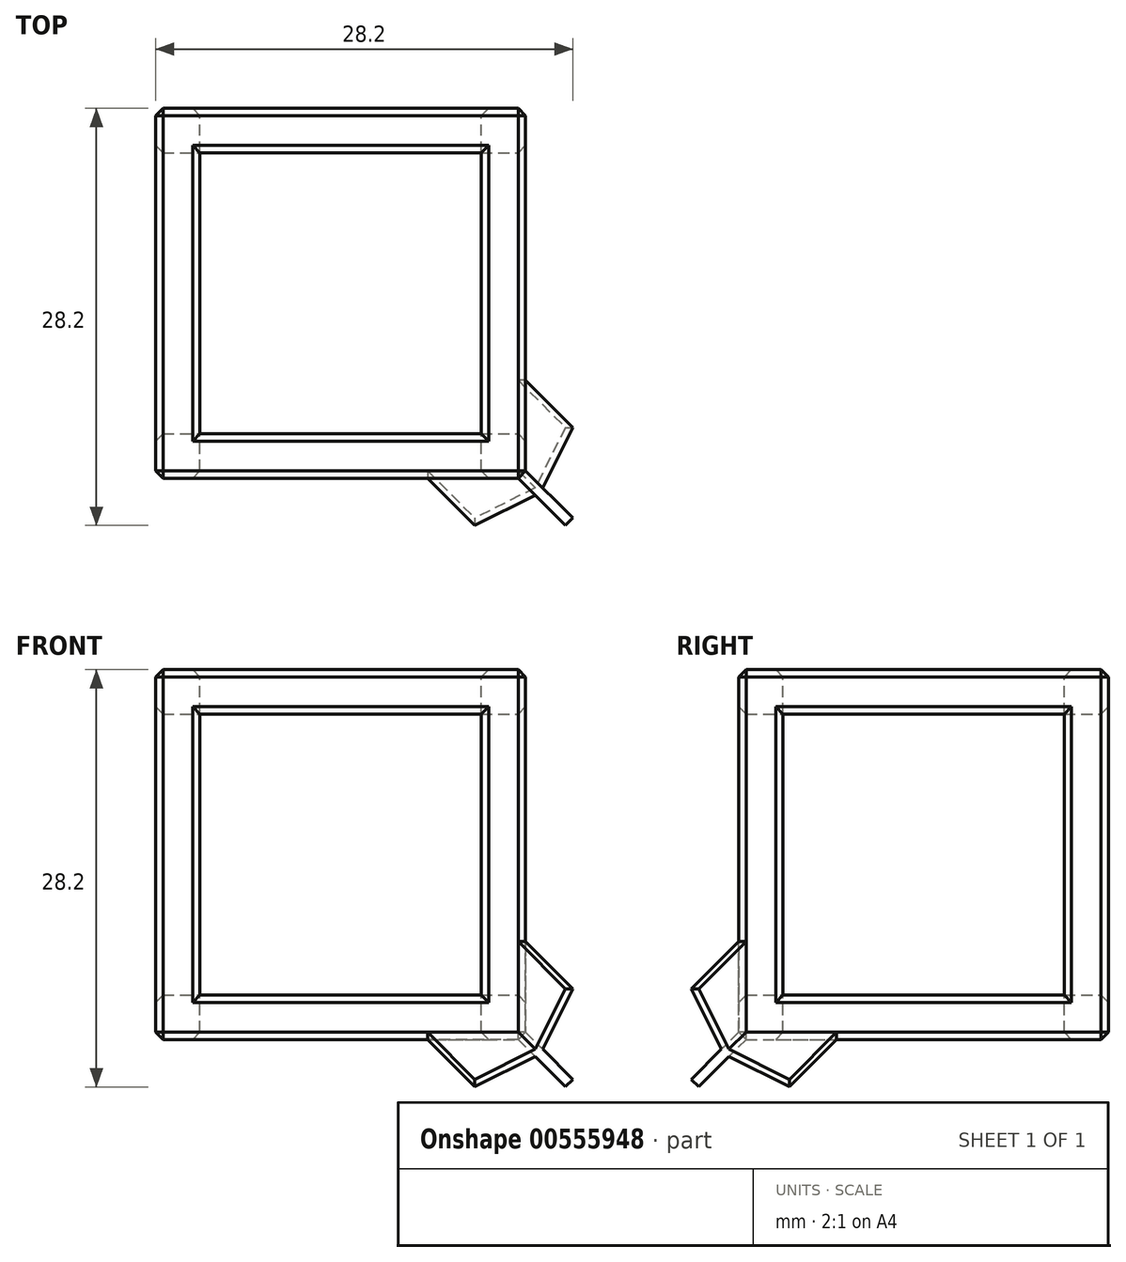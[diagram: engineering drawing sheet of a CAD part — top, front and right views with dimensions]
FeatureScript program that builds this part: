
annotation { "Feature Type Name" : "Feature", "Feature Type Description" : "" }
export const myFeature = defineFeature(function(context is Context, id is Id, definition is map)
    precondition{}
    {
        {
            var Q0;
            Q0=qCreatedBy(makeId("Front.planeOp"),FACE);
            var sketch = newSketch(context, id + "F0", { "sketchPlane" : qUnion([Q0])});
            skLineSegment(sketch, "E0.bottom", {"start": v(12.5, -12.5) * mm, "end": v(-12.5, -12.5) * mm});
            skLineSegment(sketch, "E0.top", {"start": v(12.5, 12.5) * mm, "end": v(-12.5, 12.5) * mm});
            skLineSegment(sketch, "E0.left", {"start": v(12.5, -12.5) * mm, "end": v(12.5, 12.5) * mm});
            skLineSegment(sketch, "E0.right", {"start": v(-12.5, -12.5) * mm, "end": v(-12.5, 12.5) * mm});
            skPoint(sketch, "E0.middle", {"position": v(0, 0) * mm});
            skLineSegment(sketch, "E1.0", {"start": v(9.5, -9.5) * mm, "end": v(-9.5, -9.5) * mm});
            skLineSegment(sketch, "E1.1", {"start": v(9.5, -9.5) * mm, "end": v(9.5, 9.5) * mm});
            skLineSegment(sketch, "E1.2", {"start": v(9.5, 9.5) * mm, "end": v(-9.5, 9.5) * mm});
            skLineSegment(sketch, "E1.3", {"start": v(-9.5, -9.5) * mm, "end": v(-9.5, 9.5) * mm});
            skSolve(sketch);
        }
        {
            var Q0;
            Q0=makeQuery(id+"F0.imprint","IMPRINT",FACE,{"disambiguationData":[TD([[makeQuery(id+"F0.imprint","IMPRINT",EDGE,{"derivedFrom":sQuery(id+"F0.wireOp",EDGE,"E0.bottom")}),-1.0]])]});
            extrude(context, id + "F1", {"entities" : qUnion([Q0]), "depth" : 12.5 * mm, "offsetDistance" : 25 * mm, "hasSecondDirection" : true, "secondDirectionOppositeDirection" : true, "secondDirectionDepth" : 12.5 * mm});
        }
        {
            var Q0;
            Q0=qCreatedBy(makeId("Right.planeOp"),FACE);
            var sketch = newSketch(context, id + "F2", { "sketchPlane" : qUnion([Q0])});
            skLineSegment(sketch, "E2.0", {"start": v(9.5, -9.5) * mm, "end": v(9.5, 9.5) * mm});
            skLineSegment(sketch, "E2.1", {"start": v(-9.5, -9.5) * mm, "end": v(9.5, -9.5) * mm});
            skLineSegment(sketch, "E2.2", {"start": v(-9.5, 9.5) * mm, "end": v(-9.5, -9.5) * mm});
            skLineSegment(sketch, "E2.3", {"start": v(9.5, 9.5) * mm, "end": v(-9.5, 9.5) * mm});
            skSolve(sketch);
        }
        {
            var Q0;
            Q0=makeQuery(id+"F2.imprint","IMPRINT",FACE,{"disambiguationData":[TD([[makeQuery(id+"F2.imprint","IMPRINT",EDGE,{"derivedFrom":sQuery(id+"F2.wireOp",EDGE,"E2.0")}),1.0]])]});
            extrude(context, id + "F3", {"entities" : qUnion([Q0]), "operationType" : NewBodyOperationType.REMOVE, "oppositeDirection" : true, "depth" : 25 * mm, "offsetDistance" : 25 * mm, "hasSecondDirection" : true, "secondDirectionOppositeDirection" : false, "secondDirectionDepth" : 25 * mm});
        }
        {
            var Q0;
            Q0=qCreatedBy(makeId("Top.planeOp"),FACE);
            var sketch = newSketch(context, id + "F4", { "sketchPlane" : qUnion([Q0])});
            skLineSegment(sketch, "E3.0", {"start": v(9.5, 9.5) * mm, "end": v(-9.5, 9.5) * mm});
            skLineSegment(sketch, "E3.1", {"start": v(9.5, -9.5) * mm, "end": v(9.5, 9.5) * mm});
            skLineSegment(sketch, "E3.2", {"start": v(-9.5, -9.5) * mm, "end": v(9.5, -9.5) * mm});
            skLineSegment(sketch, "E3.3", {"start": v(-9.5, 9.5) * mm, "end": v(-9.5, -9.5) * mm});
            skSolve(sketch);
        }
        {
            var Q0;
            Q0=makeQuery(id+"F4.imprint","IMPRINT",FACE,{"disambiguationData":[TD([[makeQuery(id+"F4.imprint","IMPRINT",EDGE,{"derivedFrom":sQuery(id+"F4.wireOp",EDGE,"E3.0")}),1.0]])]});
            extrude(context, id + "F5", {"entities" : qUnion([Q0]), "operationType" : NewBodyOperationType.REMOVE, "oppositeDirection" : true, "depth" : 25 * mm, "offsetDistance" : 25 * mm, "hasSecondDirection" : true, "secondDirectionOppositeDirection" : false, "secondDirectionDepth" : 25 * mm});
        }
        {
            var Q0;
            Q0=makeQuery(id+"F1.opExtrude","SWEPT_FACE",FACE,{"disambiguationData":[OSD([sQuery(id+"F0.wireOp",EDGE,"E0.left")])]});
            var Q1;
            Q1=makeQuery(id+"F1.opExtrude","SWEPT_FACE",FACE,{"disambiguationData":[OSD([sQuery(id+"F0.wireOp",EDGE,"E0.top")])]});
            var Q2;
            Q2=makeQuery(id+"F1.opExtrude","CAP_FACE",FACE,{"disambiguationData":[OSD([sQuery(id+"F0.wireOp",EDGE,"E0.bottom"),sQuery(id+"F0.wireOp",EDGE,"E0.top"),sQuery(id+"F0.wireOp",EDGE,"E0.left"),sQuery(id+"F0.wireOp",EDGE,"E0.right"),sQuery(id+"F0.wireOp",EDGE,"E1.0"),sQuery(id+"F0.wireOp",EDGE,"E1.1"),sQuery(id+"F0.wireOp",EDGE,"E1.2"),sQuery(id+"F0.wireOp",EDGE,"E1.3")])],"isStart":false});
            var Q3;
            Q3=makeQuery(id+"F1.opExtrude","CAP_FACE",FACE,{"disambiguationData":[OSD([sQuery(id+"F0.wireOp",EDGE,"E0.bottom"),sQuery(id+"F0.wireOp",EDGE,"E0.top"),sQuery(id+"F0.wireOp",EDGE,"E0.left"),sQuery(id+"F0.wireOp",EDGE,"E0.right"),sQuery(id+"F0.wireOp",EDGE,"E1.0"),sQuery(id+"F0.wireOp",EDGE,"E1.1"),sQuery(id+"F0.wireOp",EDGE,"E1.2"),sQuery(id+"F0.wireOp",EDGE,"E1.3")])],"isStart":true});
            var Q4;
            Q4=makeQuery(id+"F1.opExtrude","SWEPT_FACE",FACE,{"disambiguationData":[OSD([sQuery(id+"F0.wireOp",EDGE,"E0.right")])]});
            var Q5;
            Q5=makeQuery(id+"F1.opExtrude","SWEPT_FACE",FACE,{"disambiguationData":[OSD([sQuery(id+"F0.wireOp",EDGE,"E0.bottom")])]});
            chamfer(context, id + "F6", {"entities" : qUnion([Q0, Q1, Q2, Q3, Q4, Q5]), "width" : .5 * mm, "tangentPropagation" : true});
        }
        {
            var Q0;
            {var subQ0=sQuery(id+"F0.wireOp",EDGE,"E0.left");var subQ1=sQuery(id+"F0.wireOp",EDGE,"E0.bottom");Q0=makeQuery(id+"F6.opChamfer","BLEND_FACE",FACE,{"disambiguationData":[OSD([subQ1,subQ0]),TDD([makeQuery(id+"F1.opExtrude","CAP_VERTEX",VERTEX,{"disambiguationData":[OSD([subQ1,subQ0])],"isStart":false})])]});}
            cPlane(context, id + "F7", {"entities" : qUnion([Q0]), "cplaneType" : CPlaneType.OFFSET, "offset" : 2 * mm, "width" : 150 * mm, "height" : 150 * mm});
        }
        {
            var Q0;
            Q0=qCreatedBy(id+"F7.planeOp",FACE);
            var sketch = newSketch(context, id + "F8", { "sketchPlane" : qUnion([Q0])});
            skLineSegment(sketch, "E4.0", {"start": v(0.4, 0) * mm, "end": v(10.2, -16.97) * mm});
            skLineSegment(sketch, "E5.0", {"start": v(9.6, -17.32) * mm, "end": v(-0.2, -0.35) * mm});
            skLineSegment(sketch, "E6.0", {"start": v(-0.2, -0.35) * mm, "end": v(-19.8, -0.35) * mm});
            skLineSegment(sketch, "E7.0", {"start": v(-19.8, 0.35) * mm, "end": v(-0.2, 0.35) * mm});
            skLineSegment(sketch, "E8.0", {"start": v(-0.2, 0.35) * mm, "end": v(9.6, 17.32) * mm});
            skLineSegment(sketch, "E9.0", {"start": v(10.2, 16.97) * mm, "end": v(0.4, 0) * mm});
            skLineSegment(sketch, "E10.0", {"start": v(10.4, 0) * mm, "end": v(-5.2, 9.01) * mm});
            skLineSegment(sketch, "E10.1", {"start": v(-5.2, -9.01) * mm, "end": v(10.4, 0) * mm});
            skLineSegment(sketch, "E10.2", {"start": v(-5.2, -9.01) * mm, "end": v(-5.2, 9.01) * mm});
            skSolve(sketch);
        }
        {
            var Q0;
            {var subQ11=sQuery(id+"F8.wireOp",EDGE,"E9.0");var subQ12=sQuery(id+"F8.wireOp",EDGE,"E4.0");var subQ13=makeQuery(id+"F8.imprint","INTERSECT",VERTEX,{"derivedFrom":[subQ12,subQ11]});Q0=makeQuery(id+"F8.imprint","IMPRINT",FACE,{"disambiguationData":[TD([[makeQuery(id+"F8.imprint","IMPRINT",EDGE,{"disambiguationData":[TD([[subQ13,-1.0]])],"derivedFrom":subQ12}),-1.0]])]});}
            extrude(context, id + "F9", {"entities" : qUnion([Q0]), "operationType" : NewBodyOperationType.ADD, "endBound" : BoundingType.UP_TO_NEXT, "oppositeDirection" : true, "depth" : 25 * mm, "offsetDistance" : 25 * mm});
        }
    });
